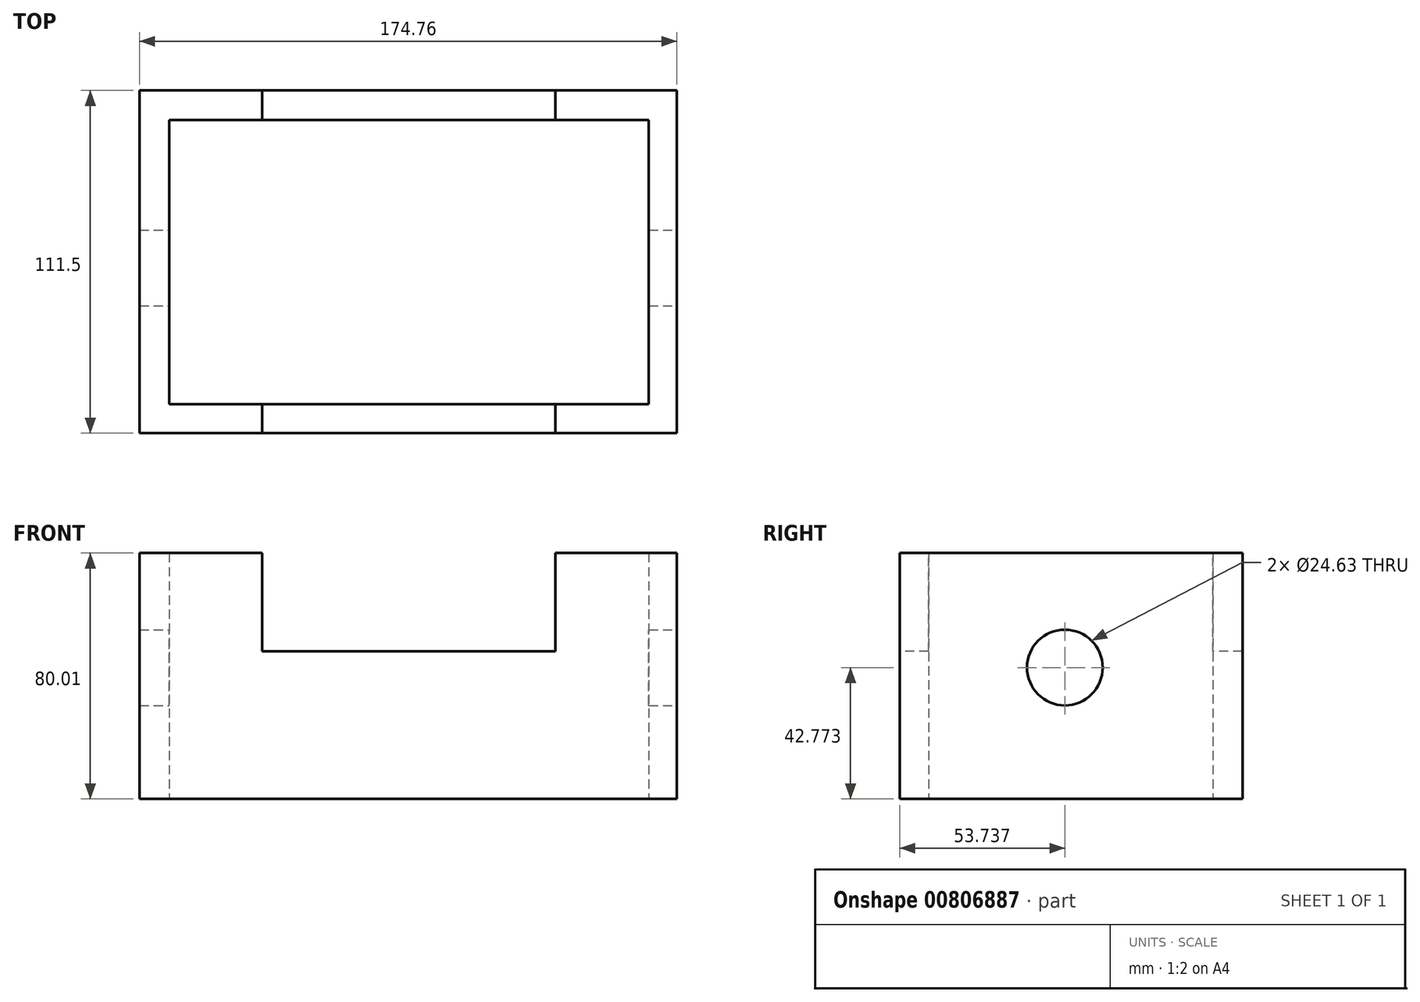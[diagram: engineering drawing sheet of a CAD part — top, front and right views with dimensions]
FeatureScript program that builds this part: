
annotation { "Feature Type Name" : "Feature", "Feature Type Description" : "" }
export const myFeature = defineFeature(function(context is Context, id is Id, definition is map)
    precondition{}
    {
        {
            var Q0;
            Q0=qCreatedBy(makeId("Top.planeOp"),FACE);
            var sketch = newSketch(context, id + "F0", { "sketchPlane" : qUnion([Q0])});
            skLineSegment(sketch, "E0.bottom", {"start": v(-75.79, 68.28) * mm, "end": v(80.21, 68.28) * mm});
            skLineSegment(sketch, "E0.top", {"start": v(-85.44, 77.93) * mm, "end": v(89.32, 77.93) * mm});
            skLineSegment(sketch, "E0.left", {"start": v(-85.44, 68.28) * mm, "end": v(-85.44, 77.93) * mm});
            skLineSegment(sketch, "E0.right", {"start": v(89.32, 68.28) * mm, "end": v(89.32, 77.93) * mm});
            skLineSegment(sketch, "E1.bottom", {"start": v(-85.44, 77.93) * mm, "end": v(-75.79, 77.93) * mm});
            skLineSegment(sketch, "E1.left", {"start": v(-85.44, 68.28) * mm, "end": v(-85.44, -24.2) * mm});
            skLineSegment(sketch, "E1.right", {"start": v(-75.79, 68.28) * mm, "end": v(-75.79, -24.2) * mm});
            skLineSegment(sketch, "E2.bottom", {"start": v(-85.44, -33.57) * mm, "end": v(89.32, -33.57) * mm});
            skLineSegment(sketch, "E2.top", {"start": v(-75.79, -24.2) * mm, "end": v(80.21, -24.2) * mm});
            skLineSegment(sketch, "E2.left", {"start": v(-85.44, -33.57) * mm, "end": v(-85.44, -24.2) * mm});
            skLineSegment(sketch, "E2.right", {"start": v(89.32, -33.57) * mm, "end": v(89.32, -24.2) * mm});
            skLineSegment(sketch, "E3.top", {"start": v(89.32, -33.57) * mm, "end": v(80.21, -33.57) * mm});
            skLineSegment(sketch, "E3.left", {"start": v(89.32, 68.28) * mm, "end": v(89.32, -33.57) * mm});
            skLineSegment(sketch, "E3.right", {"start": v(80.21, 68.28) * mm, "end": v(80.21, -24.2) * mm});
            skSolve(sketch);
        }
        {
            var Q0;
            Q0=makeQuery(id+"F0.imprint","IMPRINT",FACE,{"disambiguationData":[TD([[makeQuery(id+"F0.imprint","IMPRINT",EDGE,{"derivedFrom":sQuery(id+"F0.wireOp",EDGE,"E0.bottom")}),1.0]])]});
            extrude(context, id + "F1", {"entities" : qUnion([Q0]), "depth" : 80 * mm, "offsetDistance" : 25.4 * mm});
        }
        {
            var Q0;
            Q0=makeQuery(id+"F1.opExtrude","SWEPT_FACE",FACE,{"disambiguationData":[OSD([sQuery(id+"F0.wireOp",EDGE,"E2.bottom"),sQuery(id+"F0.wireOp",EDGE,"E3.top")])]});
            var sketch = newSketch(context, id + "F2", { "sketchPlane" : qUnion([Q0])});
            skLineSegment(sketch, "E4.top", {"start": v(-45.52, 48) * mm, "end": v(49.82, 48) * mm});
            skLineSegment(sketch, "E4.left", {"start": v(-45.52, 80) * mm, "end": v(-45.52, 48) * mm});
            skLineSegment(sketch, "E4.right", {"start": v(49.82, 80) * mm, "end": v(49.82, 48) * mm});
            skSolve(sketch);
        }
        {
            var Q0;
            Q0=makeQuery(id+"F2.imprint","IMPRINT",FACE,{"disambiguationData":[TD([[makeQuery(id+"F2.imprint","IMPRINT",EDGE,{"derivedFrom":sQuery(id+"F2.wireOp",EDGE,"E4.top")}),1.0]])]});
            extrude(context, id + "F3", {"entities" : qUnion([Q0]), "operationType" : NewBodyOperationType.REMOVE, "endBound" : BoundingType.THROUGH_ALL, "oppositeDirection" : true, "depth" : 25.4 * mm, "offsetDistance" : 25.4 * mm});
        }
        {
            var Q0;
            Q0=makeQuery(id+"F1.opExtrude","SWEPT_FACE",FACE,{"disambiguationData":[OSD([sQuery(id+"F0.wireOp",EDGE,"E0.right"),sQuery(id+"F0.wireOp",EDGE,"E3.left")])]});
            var sketch = newSketch(context, id + "F4", { "sketchPlane" : qUnion([Q0])});
            skCircle(sketch, "E5", {"center": v(20.17, 42.77) * mm, "radius": 12.31 * mm});
            skSolve(sketch);
        }
        {
            var Q0;
            Q0=makeQuery(id+"F4.imprint","IMPRINT",FACE,{"disambiguationData":[TD([[makeQuery(id+"F4.imprint","IMPRINT",EDGE,{"derivedFrom":sQuery(id+"F4.wireOp",EDGE,"E5")}),1.0]])]});
            extrude(context, id + "F5", {"entities" : qUnion([Q0]), "operationType" : NewBodyOperationType.REMOVE, "endBound" : BoundingType.THROUGH_ALL, "oppositeDirection" : true, "depth" : 25.4 * mm, "offsetDistance" : 25.4 * mm});
        }
    });
